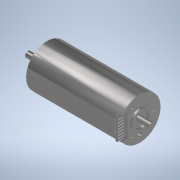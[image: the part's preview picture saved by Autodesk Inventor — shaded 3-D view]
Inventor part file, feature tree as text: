
AUTODESK INVENTOR PART (.ipt)
format: ipt  version: 2020.2 (Build 242310000, 310)  size: 642,048 bytes
history: native  units: mm
features: other x4, plane x1, extrude x1, imported_body x1, sketch x1
ambient origin geometry x8: Origin, YZ Plane, XZ Plane, XY Plane, X Axis, Y Axis, Z Axis, Center Point
bodies: Volumenkörper1 (feature_tree)
feature tree (8):
  other  "MaxonECmax22-25W"
  other  "EC-max22-2838561"
  plane  "Arbeitsebene2"
  extrude  "Extrusion1"  [1 undecoded]
  imported_body  "Basis1"
  sketch  "Skizze2"  dims[d4=10.0mm d5=0.0mm]
  other  "Zusammengesetzt1"
  other  "Fläche1"
note: 1 required parameter value undecoded (feature->parameter linkage not recoverable at this tier; creation-order binding heuristic only, values carry confidence <= 0.55)
